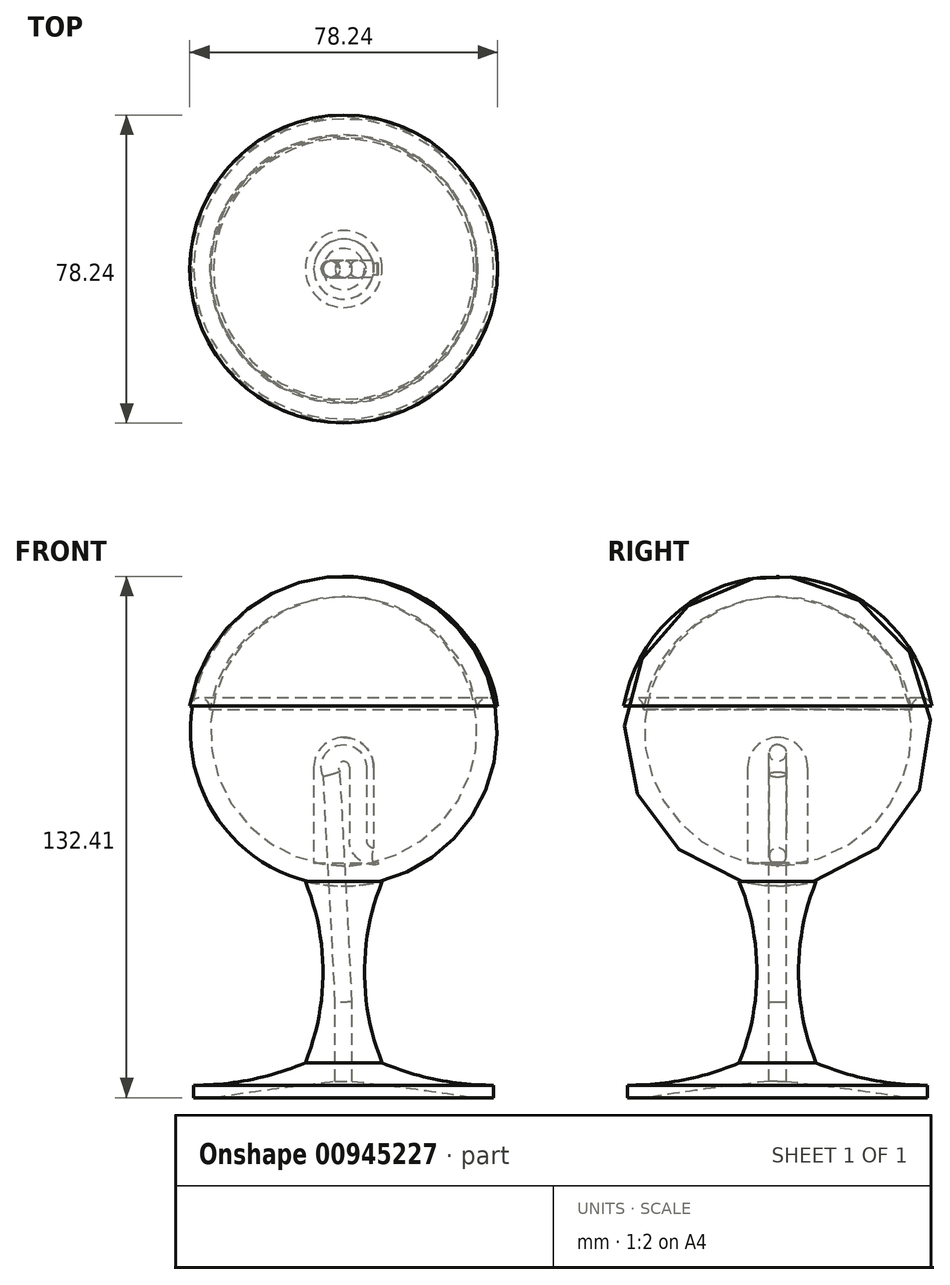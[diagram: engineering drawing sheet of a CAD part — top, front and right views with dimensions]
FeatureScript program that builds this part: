
annotation { "Feature Type Name" : "Feature", "Feature Type Description" : "" }
export const myFeature = defineFeature(function(context is Context, id is Id, definition is map)
    precondition{}
    {
        {
            var Q0;
            Q0=qCreatedBy(makeId("Front.planeOp"),FACE);
            var sketch = newSketch(context, id + "F0", { "sketchPlane" : qUnion([Q0])});
            skLineSegment(sketch, "E0", {"start": v(0, 4.4) * mm, "end": v(0, 91.52) * mm});
            skLineSegment(sketch, "E1", {"start": v(33.49, 101.6) * mm, "end": v(38.71, 101.6) * mm});
            skLineSegment(sketch, "E2", {"start": v(33.07, 0) * mm, "end": v(38.1, 0) * mm});
            skLineSegment(sketch, "E3", {"start": v(38.1, 0) * mm, "end": v(38.1, 3.18) * mm});
            skArc(sketch, "E4", {"start": v(9.77, 54.96) * mm, "mid": v(33.73, 72.39) * mm, "end": v(38.71, 101.6) * mm});
            skArc(sketch, "E5", {"start": v(9.77, 8.87) * mm, "mid": v(23.64, 4.57) * mm, "end": v(38.1, 3.17) * mm});
            skLineSegment(sketch, "E6", {"start": v(7.62, 59.67) * mm, "end": v(7.62, 83.9) * mm});
            skPoint(sketch, "E7.center.orphan", {"position": v(0, 83.9) * mm});
            skArc(sketch, "E8.0", {"start": v(7.62, 59.67) * mm, "mid": v(29.46, 75.14) * mm, "end": v(33.49, 101.6) * mm});
            skArc(sketch, "E9", {"start": v(7.62, 83.9) * mm, "mid": v(5.39, 89.29) * mm, "end": v(0, 91.52) * mm});
            skArc(sketch, "E10", {"start": v(9.77, 54.96) * mm, "mid": v(5.27, 31.91) * mm, "end": v(9.77, 8.87) * mm});
            skArc(sketch, "E11", {"start": v(33.07, 0) * mm, "mid": v(16.56, 2.43) * mm, "end": v(0, 4.4) * mm});
            skSolve(sketch);
        }
        {
            var Q0;
            Q0=qSketchRegion(id+"F0",true);
            var Q1;
            Q1=sQuery(id+"F0.wireOp",EDGE,"E0");
            revolve(context, id + "F1", {"entities" : qUnion([Q0]), "axis" : qUnion([Q1]), "revolveType" : RevolveType.FULL});
        }
        {
            var Q0;
            Q0=qCreatedBy(makeId("Front.planeOp"),FACE);
            var sketch = newSketch(context, id + "F2", { "sketchPlane" : qUnion([Q0])});
            skArc(sketch, "E12", {"start": v(3.56, 84) * mm, "mid": v(-0.97, 87.43) * mm, "end": v(-3.03, 82.12) * mm});
            skLineSegment(sketch, "E13", {"start": v(3.56, 84) * mm, "end": v(3.56, 65.45) * mm});
            skArc(sketch, "E14", {"start": v(3.56, 65.45) * mm, "mid": v(5.02, 62.3) * mm, "end": v(8.38, 61.36) * mm});
            skLineSegment(sketch, "E15", {"start": v(-3.03, 82.12) * mm, "end": v(0, 24.25) * mm});
            skLineSegment(sketch, "E16", {"start": v(0, 24.25) * mm, "end": v(0, 0) * mm});
            skSolve(sketch);
        }
        {
            var Q0;
            Q0=makeQuery(id+"F1.opRevolve","SWEPT_FACE",FACE,{"disambiguationData":[OSD([sQuery(id+"F0.wireOp",EDGE,"E2")])]});
            var sketch = newSketch(context, id + "F3", { "sketchPlane" : qUnion([Q0])});
            skCircle(sketch, "E17", {"center": v(0, 0) * mm, "radius": 2.16 * mm});
            skSolve(sketch);
        }
        {
            var Q0;
            Q0=makeQuery(id+"F3.imprint","IMPRINT",FACE,{"disambiguationData":[TD([[makeQuery(id+"F3.imprint","IMPRINT",EDGE,{"derivedFrom":sQuery(id+"F3.wireOp",EDGE,"E17")}),1.0]])]});
            var Q1;
            Q1=sQuery(id+"F2.wireOp",EDGE,"E16");
            var Q2;
            Q2=sQuery(id+"F2.wireOp",EDGE,"E15");
            var Q3;
            Q3=sQuery(id+"F2.wireOp",EDGE,"E12");
            var Q4;
            Q4=sQuery(id+"F2.wireOp",EDGE,"E13");
            var Q5;
            Q5=sQuery(id+"F2.wireOp",EDGE,"E14");
            sweep(context, id + "F4", {"operationType" : NewBodyOperationType.REMOVE, "profiles" : qUnion([Q0]), "path" : qUnion([Q1, Q2, Q3, Q4, Q5])});
        }
        {
            var Q0;
            Q0=makeQuery(id+"F1.opRevolve","SWEPT_EDGE",EDGE,{"disambiguationData":[OSD([sQuery(id+"F0.wireOp",EDGE,"E1"),sQuery(id+"F0.wireOp",EDGE,"E8.0")])]});
            var Q1;
            Q1=makeQuery(id+"F1.opRevolve","SWEPT_EDGE",EDGE,{"disambiguationData":[OSD([sQuery(id+"F0.wireOp",EDGE,"E1"),sQuery(id+"F0.wireOp",EDGE,"E4")])]});
            var Q2;
            Q2=makeQuery(id+"FxQKJDNVuqQIBrW_1.opRevolve","SWEPT_EDGE",EDGE,{"disambiguationData":[OSD([sQuery(id+"F0.wireOp",EDGE,"E1"),sQuery(id+"F0.wireOp",EDGE,"E8.0")])]});
            var Q3;
            Q3=makeQuery(id+"FxQKJDNVuqQIBrW_1.opRevolve","SWEPT_EDGE",EDGE,{"disambiguationData":[OSD([sQuery(id+"F0.wireOp",EDGE,"E1"),sQuery(id+"F0.wireOp",EDGE,"E4")])]});
            fillet(context, id + "F5", {"entities" : qUnion([Q0, Q1, Q2, Q3]), "radius" : 2.54 * mm, "tangentPropagation" : true, "allowEdgeOverflow" : false});
        }
    });
